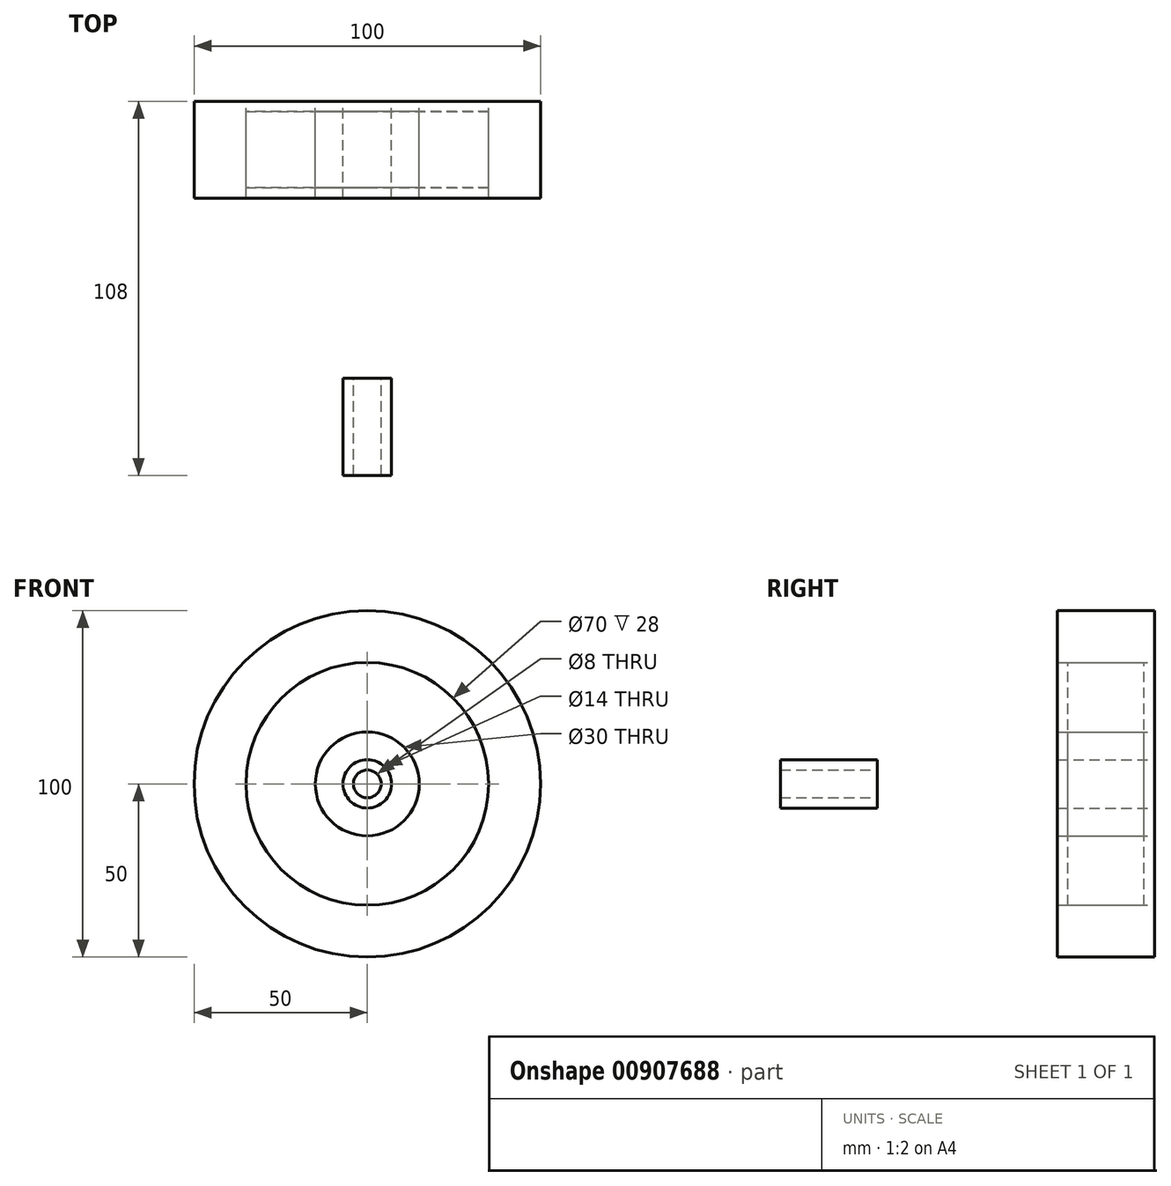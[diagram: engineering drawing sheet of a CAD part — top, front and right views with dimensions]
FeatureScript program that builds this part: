
annotation { "Feature Type Name" : "Feature", "Feature Type Description" : "" }
export const myFeature = defineFeature(function(context is Context, id is Id, definition is map)
    precondition{}
    {
        {
            var Q0;
            Q0=qCreatedBy(makeId("Front.planeOp"),FACE);
            var sketch = newSketch(context, id + "F0", { "sketchPlane" : qUnion([Q0])});
            skCircle(sketch, "E0", {"center": v(0, 0) * mm, "radius": 7 * mm});
            skCircle(sketch, "E1", {"center": v(0, 0) * mm, "radius": 15 * mm});
            skSolve(sketch);
        }
        {
            var Q0;
            Q0=makeQuery(id+"F0.imprint","IMPRINT",FACE,{"disambiguationData":[TD([[makeQuery(id+"F0.imprint","IMPRINT",EDGE,{"derivedFrom":sQuery(id+"F0.wireOp",EDGE,"E0")}),-1.0]])]});
            var Q1;
            Q1=sQuery(id+"F0.wireOp",EDGE,"E0");
            var Q2;
            Q2=sQuery(id+"F0.wireOp",EDGE,"E1");
            extrude(context, id + "F1", {"entities" : qUnion([Q0]), "surfaceEntities" : qUnion([Q1, Q2]), "depth" : 28 * mm, "offsetDistance" : 25 * mm});
        }
        {
            var Q0;
            Q0=qCreatedBy(makeId("Front.planeOp"),FACE);
            var sketch = newSketch(context, id + "F2", { "sketchPlane" : qUnion([Q0])});
            skCircle(sketch, "E2", {"center": v(0, 0) * mm, "radius": 35 * mm});
            skCircle(sketch, "E3", {"center": v(0, 0) * mm, "radius": 50 * mm});
            skSolve(sketch);
        }
        {
            var Q0;
            Q0=makeQuery(id+"F2.imprint","IMPRINT",FACE,{"disambiguationData":[TD([[makeQuery(id+"F2.imprint","IMPRINT",EDGE,{"derivedFrom":sQuery(id+"F2.wireOp",EDGE,"E2")}),-1.0]])]});
            extrude(context, id + "F3", {"entities" : qUnion([Q0]), "depth" : 28 * mm, "offsetDistance" : 25 * mm});
        }
        {
            var Q0;
            Q0=qCreatedBy(makeId("Front.planeOp"),FACE);
            cPlane(context, id + "F4", {"entities" : qUnion([Q0]), "cplaneType" : CPlaneType.OFFSET, "offset" : 14 * mm, "width" : 150 * mm, "height" : 150 * mm});
        }
        {
            var Q0;
            Q0=qCreatedBy(makeId("Front.planeOp"),FACE);
            cPlane(context, id + "F5", {"entities" : qUnion([Q0]), "cplaneType" : CPlaneType.OFFSET, "offset" : 3 * mm, "width" : 150 * mm, "height" : 150 * mm});
        }
        {
            var Q0;
            Q0=qCreatedBy(id+"F5.planeOp",FACE);
            var sketch = newSketch(context, id + "F6", { "sketchPlane" : qUnion([Q0])});
            skCircle(sketch, "E4", {"center": v(0, 0) * mm, "radius": 35 * mm});
            skCircle(sketch, "E5", {"center": v(0, 0) * mm, "radius": 15 * mm});
            skSolve(sketch);
        }
        {
            var Q0;
            Q0=makeQuery(id+"F6.imprint","IMPRINT",FACE,{"disambiguationData":[TD([[makeQuery(id+"F6.imprint","IMPRINT",EDGE,{"derivedFrom":sQuery(id+"F6.wireOp",EDGE,"E4")}),1.0]])]});
            extrude(context, id + "F7", {"entities" : qUnion([Q0]), "depth" : 22 * mm, "offsetDistance" : 25 * mm});
        }
        {
            var Q0;
            Q0=qCreatedBy(makeId("Front.planeOp"),FACE);
            cPlane(context, id + "F8", {"entities" : qUnion([Q0]), "cplaneType" : CPlaneType.OFFSET, "offset" : 80 * mm, "width" : 150 * mm, "height" : 150 * mm});
        }
        {
            var Q0;
            Q0=qCreatedBy(id+"F8.planeOp",FACE);
            var sketch = newSketch(context, id + "F9", { "sketchPlane" : qUnion([Q0])});
            skCircle(sketch, "E6", {"center": v(0, 0) * mm, "radius": 4 * mm});
            skCircle(sketch, "E7", {"center": v(0, 0) * mm, "radius": 7 * mm});
            skSolve(sketch);
        }
        {
            var Q0;
            Q0=makeQuery(id+"F9.imprint","IMPRINT",FACE,{"disambiguationData":[TD([[makeQuery(id+"F9.imprint","IMPRINT",EDGE,{"derivedFrom":sQuery(id+"F9.wireOp",EDGE,"E6")}),-1.0]])]});
            var Q1;
            Q1=sQuery(id+"F9.wireOp",EDGE,"E7");
            var Q2;
            Q2=sQuery(id+"F9.wireOp",EDGE,"E6");
            extrude(context, id + "F10", {"entities" : qUnion([Q0]), "surfaceEntities" : qUnion([Q1, Q2]), "depth" : 28 * mm, "offsetDistance" : 25 * mm});
        }
    });
